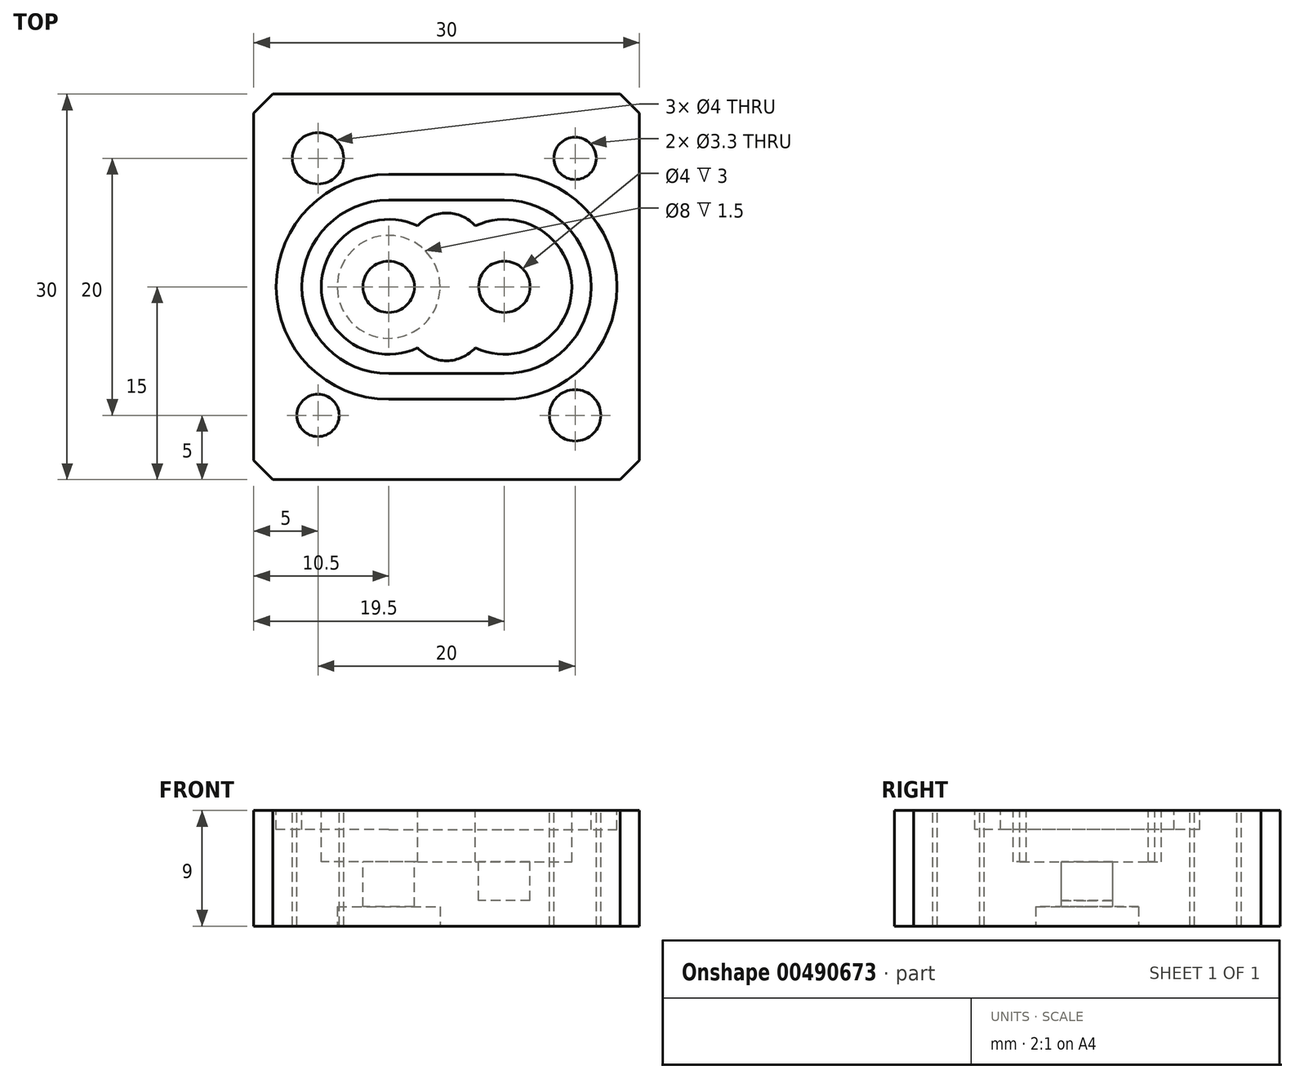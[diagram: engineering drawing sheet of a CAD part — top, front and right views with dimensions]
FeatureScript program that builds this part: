
annotation { "Feature Type Name" : "Feature", "Feature Type Description" : "" }
export const myFeature = defineFeature(function(context is Context, id is Id, definition is map)
    precondition{}
    {
        {
            var Q0;
            Q0=qCreatedBy(makeId("Top.planeOp"),FACE);
            var sketch = newSketch(context, id + "F0", { "sketchPlane" : qUnion([Q0])});
            skLineSegment(sketch, "E0.bottom", {"start": v(0, 0) * mm, "end": v(30, 0) * mm});
            skLineSegment(sketch, "E0.top", {"start": v(0, -30) * mm, "end": v(30, -30) * mm});
            skLineSegment(sketch, "E0.left", {"start": v(0, 0) * mm, "end": v(0, -30) * mm});
            skLineSegment(sketch, "E0.right", {"start": v(30, 0) * mm, "end": v(30, -30) * mm});
            skLineSegment(sketch, "E1", {"start": v(0, -15) * mm, "end": v(30, -15) * mm, "construction": true});
            skArc(sketch, "E2", {"start": v(17.24, -19.74) * mm, "mid": v(24.75, -15) * mm, "end": v(17.24, -10.26) * mm});
            skCircle(sketch, "E3", {"center": v(10.5, -15) * mm, "radius": 2 * mm});
            skCircle(sketch, "E4", {"center": v(19.5, -15) * mm, "radius": 2 * mm});
            skPoint(sketch, "E5", {"position": v(15, -15) * mm});
            skArc(sketch, "E6", {"start": v(10.5, -8.25) * mm, "mid": v(3.75, -15) * mm, "end": v(10.5, -21.75) * mm});
            skArc(sketch, "E7", {"start": v(19.5, -21.75) * mm, "mid": v(26.25, -15) * mm, "end": v(19.5, -8.25) * mm});
            skLineSegment(sketch, "E8", {"start": v(10.5, -8.25) * mm, "end": v(19.5, -8.25) * mm});
            skLineSegment(sketch, "E9", {"start": v(10.5, -21.75) * mm, "end": v(19.5, -21.75) * mm});
            skLineSegment(sketch, "E10.0", {"start": v(10.5, -23.75) * mm, "end": v(19.5, -23.75) * mm});
            skArc(sketch, "E10.1", {"start": v(10.5, -6.25) * mm, "mid": v(1.75, -15) * mm, "end": v(10.5, -23.75) * mm});
            skLineSegment(sketch, "E10.2", {"start": v(10.5, -6.25) * mm, "end": v(19.5, -6.25) * mm});
            skArc(sketch, "E10.3", {"start": v(19.5, -23.75) * mm, "mid": v(28.25, -15) * mm, "end": v(19.5, -6.25) * mm});
            skLineSegment(sketch, "E11", {"start": v(0, -12.25) * mm, "end": v(30, -12.25) * mm, "construction": true});
            skLineSegment(sketch, "E12", {"start": v(0, -17.75) * mm, "end": v(30, -17.75) * mm, "construction": true});
            skArc(sketch, "E13", {"start": v(17.24, -10.26) * mm, "mid": v(15, -9.25) * mm, "end": v(12.76, -10.26) * mm});
            skArc(sketch, "E14", {"start": v(12.76, -19.74) * mm, "mid": v(15, -20.75) * mm, "end": v(17.24, -19.74) * mm});
            skArc(sketch, "E15.trimOffspring", {"start": v(12.76, -10.26) * mm, "mid": v(5.25, -15) * mm, "end": v(12.76, -19.74) * mm});
            skArc(sketch, "E16.0", {"start": v(10.5, -7.25) * mm, "mid": v(2.75, -15) * mm, "end": v(10.5, -22.75) * mm, "construction": true});
            skLineSegment(sketch, "E16.1", {"start": v(10.5, -7.25) * mm, "end": v(19.5, -7.25) * mm, "construction": true});
            skArc(sketch, "E16.2", {"start": v(19.5, -22.75) * mm, "mid": v(27.25, -15) * mm, "end": v(19.5, -7.25) * mm, "construction": true});
            skLineSegment(sketch, "E16.3", {"start": v(10.5, -22.75) * mm, "end": v(19.5, -22.75) * mm, "construction": true});
            skLineSegment(sketch, "E17", {"start": v(15, -30) * mm, "end": v(15, 0) * mm, "construction": true});
            skLineSegment(sketch, "E18", {"start": v(0, -25) * mm, "end": v(30, -25) * mm, "construction": true});
            skLineSegment(sketch, "E19", {"start": v(0, -5) * mm, "end": v(30, -5) * mm, "construction": true});
            skLineSegment(sketch, "E20", {"start": v(5, -30) * mm, "end": v(5, 0) * mm, "construction": true});
            skLineSegment(sketch, "E21", {"start": v(25, -30) * mm, "end": v(25, 0) * mm, "construction": true});
            skCircle(sketch, "E22", {"center": v(5, -25) * mm, "radius": 1.65 * mm});
            skCircle(sketch, "E23", {"center": v(5, -5) * mm, "radius": 2 * mm});
            skCircle(sketch, "E24", {"center": v(25, -25) * mm, "radius": 2 * mm});
            skCircle(sketch, "E25", {"center": v(25, -5) * mm, "radius": 1.65 * mm});
            skSolve(sketch);
        }
        {
            var Q0;
            Q0=makeQuery(id+"F0.imprint","IMPRINT",FACE,{"disambiguationData":[TD([[makeQuery(id+"F0.imprint","IMPRINT",EDGE,{"derivedFrom":sQuery(id+"F0.wireOp",EDGE,"E0.bottom")}),-1.0]])]});
            var Q1;
            Q1=makeQuery(id+"F0.imprint","IMPRINT",FACE,{"disambiguationData":[TD([[makeQuery(id+"F0.imprint","IMPRINT",EDGE,{"derivedFrom":sQuery(id+"F0.wireOp",EDGE,"MZw8L1mY-04MB-L0nq-oH4W-q9KqwQQnYDyC")}),-1.0]])]});
            var Q2;
            Q2=makeQuery(id+"F0.imprint","IMPRINT",FACE,{"disambiguationData":[TD([[makeQuery(id+"F0.imprint","IMPRINT",EDGE,{"derivedFrom":sQuery(id+"F0.wireOp",EDGE,"MZw8L1mY-04MB-L0nq-oH4W-q9KqwQQnYDyC")}),1.0]])]});
            var Q3;
            Q3=makeQuery(id+"F0.imprint","IMPRINT",FACE,{"disambiguationData":[TD([[makeQuery(id+"F0.imprint","IMPRINT",EDGE,{"derivedFrom":sQuery(id+"F0.wireOp",EDGE,"E4")}),1.0]])]});
            var Q4;
            Q4=makeQuery(id+"F0.imprint","IMPRINT",FACE,{"disambiguationData":[TD([[makeQuery(id+"F0.imprint","IMPRINT",EDGE,{"derivedFrom":sQuery(id+"F0.wireOp",EDGE,"E6")}),-1.0]])]});
            var Q5;
            Q5=makeQuery(id+"F0.imprint","IMPRINT",FACE,{"disambiguationData":[TD([[makeQuery(id+"F0.imprint","IMPRINT",EDGE,{"derivedFrom":sQuery(id+"F0.wireOp",EDGE,"E2")}),1.0]])]});
            var Q6;
            Q6=makeQuery(id+"F0.imprint","IMPRINT",FACE,{"disambiguationData":[TD([[makeQuery(id+"F0.imprint","IMPRINT",EDGE,{"derivedFrom":sQuery(id+"F0.wireOp",EDGE,"E2")}),-1.0]])]});
            var Q7;
            Q7=makeQuery(id+"F0.imprint","IMPRINT",FACE,{"disambiguationData":[TD([[makeQuery(id+"F0.imprint","IMPRINT",EDGE,{"derivedFrom":sQuery(id+"F0.wireOp",EDGE,"ea91da5f-1847-4e72-b56f-cc8c6eb2f272.0.1.0")}),1.0]])]});
            var Q8;
            Q8=makeQuery(id+"F0.imprint","IMPRINT",FACE,{"disambiguationData":[TD([[makeQuery(id+"F0.imprint","IMPRINT",EDGE,{"derivedFrom":sQuery(id+"F0.wireOp",EDGE,"ea91da5f-1847-4e72-b56f-cc8c6eb2f272.1.0.0")}),1.0]])]});
            var Q9;
            Q9=makeQuery(id+"F0.imprint","IMPRINT",FACE,{"disambiguationData":[TD([[makeQuery(id+"F0.imprint","IMPRINT",EDGE,{"derivedFrom":sQuery(id+"F0.wireOp",EDGE,"E25")}),1.0]])]});
            var Q10;
            Q10=makeQuery(id+"F0.imprint","IMPRINT",FACE,{"disambiguationData":[TD([[makeQuery(id+"F0.imprint","IMPRINT",EDGE,{"derivedFrom":sQuery(id+"F0.wireOp",EDGE,"E24")}),1.0]])]});
            extrude(context, id + "F1", {"entities" : qUnion([Q0, Q1, Q2, Q3, Q4, Q5, Q6, Q7, Q8, Q9, Q10]), "oppositeDirection" : true, "depth" : 9 * mm, "offsetDistance" : 25 * mm});
        }
        {
            var Q0;
            Q0=makeQuery(id+"F0.imprint","IMPRINT",FACE,{"disambiguationData":[TD([[makeQuery(id+"F0.imprint","IMPRINT",EDGE,{"derivedFrom":sQuery(id+"F0.wireOp",EDGE,"E6")}),-1.0]])]});
            extrude(context, id + "F2", {"entities" : qUnion([Q0]), "operationType" : NewBodyOperationType.REMOVE, "oppositeDirection" : true, "depth" : 1.5 * mm, "offsetDistance" : 25 * mm});
        }
        {
            var Q0;
            Q0=makeQuery(id+"F0.imprint","IMPRINT",FACE,{"disambiguationData":[TD([[makeQuery(id+"F0.imprint","IMPRINT",EDGE,{"derivedFrom":sQuery(id+"F0.wireOp",EDGE,"E4")}),1.0]])]});
            extrude(context, id + "F3", {"entities" : qUnion([Q0]), "operationType" : NewBodyOperationType.REMOVE, "oppositeDirection" : true, "depth" : 7 * mm, "offsetDistance" : 25 * mm});
        }
        {
            var Q0;
            Q0=makeQuery(id+"F0.imprint","IMPRINT",FACE,{"disambiguationData":[TD([[makeQuery(id+"F0.imprint","IMPRINT",EDGE,{"derivedFrom":sQuery(id+"F0.wireOp",EDGE,"E2")}),1.0]])]});
            extrude(context, id + "F4", {"entities" : qUnion([Q0]), "operationType" : NewBodyOperationType.REMOVE, "oppositeDirection" : true, "depth" : 4 * mm, "offsetDistance" : 25 * mm});
        }
        {
            var Q0;
            Q0=makeQuery(id+"F1.opExtrude","CAP_FACE",FACE,{"disambiguationData":[OSD([sQuery(id+"F0.wireOp",EDGE,"E0.bottom"),sQuery(id+"F0.wireOp",EDGE,"E0.top"),sQuery(id+"F0.wireOp",EDGE,"E0.left"),sQuery(id+"F0.wireOp",EDGE,"E0.right"),sQuery(id+"F0.wireOp",EDGE,"E3"),sQuery(id+"F0.wireOp",EDGE,"0gURjQAW-o9TF-LYW3-5VQh-sVZyAbxpT9Lx"),sQuery(id+"F0.wireOp",EDGE,"ea91da5f-1847-4e72-b56f-cc8c6eb2f272.0.1.0"),sQuery(id+"F0.wireOp",EDGE,"ea91da5f-1847-4e72-b56f-cc8c6eb2f272.1.0.0"),sQuery(id+"F0.wireOp",EDGE,"ea91da5f-1847-4e72-b56f-cc8c6eb2f272.1.1.0")])],"isStart":false});
            var sketch = newSketch(context, id + "F5", { "sketchPlane" : qUnion([Q0])});
            skLineSegment(sketch, "E26", {"start": v(15, 0) * mm, "end": v(15, 30) * mm, "construction": true});
            skCircle(sketch, "E27", {"center": v(15, 3) * mm, "radius": 1.25 * mm});
            skCircle(sketch, "E28", {"center": v(15, 27) * mm, "radius": 1.25 * mm});
            skCircle(sketch, "E29", {"center": v(10.5, 15) * mm, "radius": 4 * mm});
            skSolve(sketch);
        }
        {
            var Q0;
            Q0=makeQuery(id+"F5.imprint","IMPRINT",FACE,{"disambiguationData":[TD([[makeQuery(id+"F5.imprint","IMPRINT",EDGE,{"derivedFrom":sQuery(id+"F5.wireOp",EDGE,"E29")}),1.0]])]});
            extrude(context, id + "F6", {"entities" : qUnion([Q0]), "operationType" : NewBodyOperationType.REMOVE, "oppositeDirection" : true, "depth" : 1.5 * mm, "offsetDistance" : 25 * mm});
        }
        {
            var Q0;
            Q0=makeQuery(id+"F0.imprint","IMPRINT",FACE,{"disambiguationData":[TD([[makeQuery(id+"F0.imprint","IMPRINT",EDGE,{"derivedFrom":sQuery(id+"F0.wireOp",EDGE,"E24")}),1.0]])]});
            var Q1;
            Q1=makeQuery(id+"F0.imprint","IMPRINT",FACE,{"disambiguationData":[TD([[makeQuery(id+"F0.imprint","IMPRINT",EDGE,{"derivedFrom":sQuery(id+"F0.wireOp",EDGE,"E25")}),1.0]])]});
            extrude(context, id + "F7", {"entities" : qUnion([Q0, Q1]), "operationType" : NewBodyOperationType.REMOVE, "oppositeDirection" : true, "depth" : 10 * mm, "offsetDistance" : 25 * mm});
        }
        {
            var Q0;
            Q0=makeQuery(id+"F1.opExtrude","SWEPT_EDGE",EDGE,{"disambiguationData":[OSD([sQuery(id+"F0.wireOp",EDGE,"E0.top"),sQuery(id+"F0.wireOp",EDGE,"E0.right")])]});
            var Q1;
            Q1=makeQuery(id+"F1.opExtrude","SWEPT_EDGE",EDGE,{"disambiguationData":[OSD([sQuery(id+"F0.wireOp",EDGE,"E0.bottom"),sQuery(id+"F0.wireOp",EDGE,"E0.right")])]});
            var Q2;
            Q2=makeQuery(id+"F1.opExtrude","SWEPT_EDGE",EDGE,{"disambiguationData":[OSD([sQuery(id+"F0.wireOp",EDGE,"E0.top"),sQuery(id+"F0.wireOp",EDGE,"E0.left")])]});
            var Q3;
            Q3=makeQuery(id+"F1.opExtrude","SWEPT_EDGE",EDGE,{"disambiguationData":[OSD([sQuery(id+"F0.wireOp",EDGE,"E0.bottom"),sQuery(id+"F0.wireOp",EDGE,"E0.left")])]});
            chamfer(context, id + "F8", {"entities" : qUnion([Q0, Q1, Q2, Q3]), "width" : 1.5 * mm, "tangentPropagation" : true});
        }
    });
